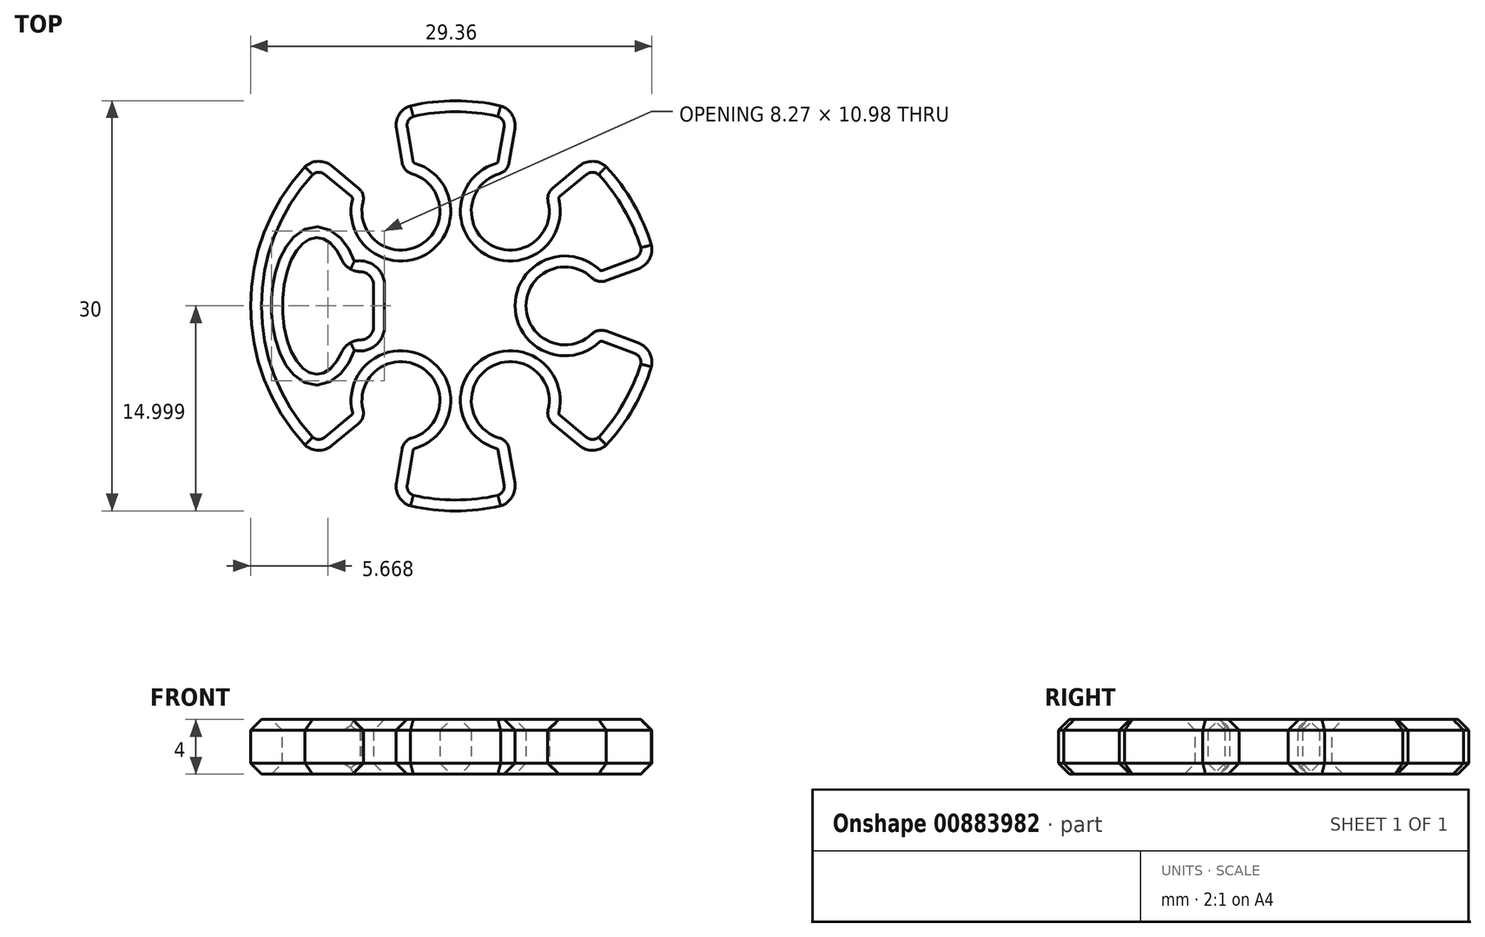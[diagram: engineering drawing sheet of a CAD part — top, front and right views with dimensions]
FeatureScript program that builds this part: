
annotation { "Feature Type Name" : "Feature", "Feature Type Description" : "" }
export const myFeature = defineFeature(function(context is Context, id is Id, definition is map)
    precondition{}
    {
        {
            var Q0;
            Q0=qCreatedBy(makeId("Top.planeOp"),FACE);
            var sketch = newSketch(context, id + "F0", { "sketchPlane" : qUnion([Q0])});
            skArc(sketch, "E0", {"start": v(9.97, 2.06) * mm, "mid": v(5.15, 0) * mm, "end": v(9.97, -2.06) * mm});
            skLineSegment(sketch, "E1", {"start": v(11.01, 1.84) * mm, "end": v(13.38, 2.73) * mm});
            skLineSegment(sketch, "E2", {"start": v(11.01, -1.84) * mm, "end": v(13.38, -2.73) * mm});
            skPoint(sketch, "E3.visualSharp", {"position": v(10.36, 1.6) * mm});
            skArc(sketch, "E3.filletArc", {"start": v(9.97, 2.06) * mm, "mid": v(10.46, 1.8) * mm, "end": v(11.01, 1.84) * mm});
            skPoint(sketch, "E4.visualSharp", {"position": v(14.65, 3.2) * mm});
            skArc(sketch, "E4.filletArc", {"start": v(13.38, 2.73) * mm, "mid": v(14.18, 3.42) * mm, "end": v(14.32, 4.46) * mm});
            skPoint(sketch, "E5.visualSharp", {"position": v(10.36, -1.6) * mm});
            skArc(sketch, "E5.filletArc", {"start": v(11.01, -1.84) * mm, "mid": v(10.46, -1.8) * mm, "end": v(9.97, -2.06) * mm});
            skPoint(sketch, "E6.visualSharp", {"position": v(14.65, -3.2) * mm});
            skArc(sketch, "E6.filletArc", {"start": v(14.32, -4.46) * mm, "mid": v(14.18, -3.42) * mm, "end": v(13.38, -2.73) * mm});
            skLineSegment(sketch, "E7", {"start": v(0, 0) * mm, "end": v(8, 0) * mm, "construction": true});
            skPoint(sketch, "E8.1.0", {"position": v(6.56, 8.17) * mm});
            skPoint(sketch, "E8.1.1", {"position": v(4.56, 14.3) * mm});
            skLineSegment(sketch, "E8.1.2", {"start": v(3.9, 10.46) * mm, "end": v(4.33, 12.95) * mm});
            skLineSegment(sketch, "E8.1.3", {"start": v(0, 0) * mm, "end": v(4, 6.93) * mm, "construction": true});
            skArc(sketch, "E8.1.4", {"start": v(3.2, 9.66) * mm, "mid": v(2.57, 4.46) * mm, "end": v(6.77, 7.6) * mm});
            skPoint(sketch, "E8.1.5", {"position": v(10.1, 11.1) * mm});
            skLineSegment(sketch, "E8.1.6", {"start": v(7.1, 8.61) * mm, "end": v(9.05, 10.23) * mm});
            skArc(sketch, "E8.1.7", {"start": v(11.02, 10.18) * mm, "mid": v(10.05, 10.57) * mm, "end": v(9.05, 10.23) * mm});
            skPoint(sketch, "E8.1.8", {"position": v(3.8, 9.77) * mm});
            skArc(sketch, "E8.1.9", {"start": v(4.33, 12.95) * mm, "mid": v(4.13, 13.98) * mm, "end": v(3.3, 14.63) * mm});
            skArc(sketch, "E8.1.10", {"start": v(3.2, 9.66) * mm, "mid": v(3.67, 9.96) * mm, "end": v(3.9, 10.46) * mm});
            skArc(sketch, "E8.1.11", {"start": v(7.1, 8.61) * mm, "mid": v(6.8, 8.16) * mm, "end": v(6.77, 7.6) * mm});
            skPoint(sketch, "E8.2.0", {"position": v(-3.8, 9.77) * mm});
            skPoint(sketch, "E8.2.1", {"position": v(-10.1, 11.1) * mm});
            skLineSegment(sketch, "E8.2.2", {"start": v(-7.1, 8.61) * mm, "end": v(-9.05, 10.23) * mm});
            skLineSegment(sketch, "E8.2.3", {"start": v(0, 0) * mm, "end": v(-4, 6.93) * mm, "construction": true});
            skArc(sketch, "E8.2.4", {"start": v(-6.77, 7.6) * mm, "mid": v(-2.57, 4.46) * mm, "end": v(-3.2, 9.66) * mm});
            skPoint(sketch, "E8.2.5", {"position": v(-4.56, 14.3) * mm});
            skLineSegment(sketch, "E8.2.6", {"start": v(-3.9, 10.46) * mm, "end": v(-4.33, 12.95) * mm});
            skArc(sketch, "E8.2.7", {"start": v(-3.3, 14.63) * mm, "mid": v(-4.13, 13.98) * mm, "end": v(-4.33, 12.95) * mm});
            skPoint(sketch, "E8.2.8", {"position": v(-6.56, 8.17) * mm});
            skArc(sketch, "E8.2.9", {"start": v(-9.05, 10.23) * mm, "mid": v(-10.05, 10.57) * mm, "end": v(-11.02, 10.18) * mm});
            skArc(sketch, "E8.2.10", {"start": v(-6.77, 7.6) * mm, "mid": v(-6.8, 8.16) * mm, "end": v(-7.1, 8.61) * mm});
            skArc(sketch, "E8.2.11", {"start": v(-3.9, 10.46) * mm, "mid": v(-3.67, 9.96) * mm, "end": v(-3.2, 9.66) * mm});
            skPoint(sketch, "E8.center", {"position": v(0, 0) * mm});
            skPoint(sketch, "E9.1.4.0", {"position": v(-4.56, -14.3) * mm});
            skLineSegment(sketch, "E9.2.4.0", {"start": v(-3.9, -10.46) * mm, "end": v(-4.33, -12.95) * mm});
            skLineSegment(sketch, "E9.5.4.0", {"start": v(0, 0) * mm, "end": v(-4, -6.93) * mm, "construction": true});
            skPoint(sketch, "E9.7.4.0", {"position": v(-6.56, -8.17) * mm});
            skArc(sketch, "E9.8.4.0", {"start": v(-3.2, -9.66) * mm, "mid": v(-2.58, -4.46) * mm, "end": v(-6.77, -7.6) * mm});
            skPoint(sketch, "E9.12.4.0", {"position": v(-10.1, -11.1) * mm});
            skLineSegment(sketch, "E9.13.4.0", {"start": v(-7.1, -8.61) * mm, "end": v(-9.05, -10.23) * mm});
            skArc(sketch, "E9.16.4.0", {"start": v(-11.02, -10.18) * mm, "mid": v(-10.05, -10.57) * mm, "end": v(-9.05, -10.23) * mm});
            skPoint(sketch, "E9.20.4.0", {"position": v(-3.8, -9.77) * mm});
            skArc(sketch, "E9.21.4.0", {"start": v(-4.33, -12.95) * mm, "mid": v(-4.13, -13.98) * mm, "end": v(-3.3, -14.63) * mm});
            skArc(sketch, "E9.25.4.0", {"start": v(-3.2, -9.66) * mm, "mid": v(-3.67, -9.96) * mm, "end": v(-3.9, -10.46) * mm});
            skArc(sketch, "E9.29.4.0", {"start": v(-7.1, -8.61) * mm, "mid": v(-6.8, -8.16) * mm, "end": v(-6.77, -7.6) * mm});
            skPoint(sketch, "E9.1.5.0", {"position": v(10.1, -11.1) * mm});
            skLineSegment(sketch, "E9.2.5.0", {"start": v(7.1, -8.61) * mm, "end": v(9.05, -10.23) * mm});
            skLineSegment(sketch, "E9.5.5.0", {"start": v(0, 0) * mm, "end": v(4, -6.93) * mm, "construction": true});
            skPoint(sketch, "E9.7.5.0", {"position": v(3.8, -9.77) * mm});
            skArc(sketch, "E9.8.5.0", {"start": v(6.77, -7.6) * mm, "mid": v(2.57, -4.46) * mm, "end": v(3.2, -9.66) * mm});
            skPoint(sketch, "E9.12.5.0", {"position": v(4.56, -14.3) * mm});
            skLineSegment(sketch, "E9.13.5.0", {"start": v(3.9, -10.46) * mm, "end": v(4.33, -12.95) * mm});
            skArc(sketch, "E9.16.5.0", {"start": v(3.3, -14.63) * mm, "mid": v(4.13, -13.98) * mm, "end": v(4.33, -12.95) * mm});
            skPoint(sketch, "E9.20.5.0", {"position": v(6.56, -8.17) * mm});
            skArc(sketch, "E9.21.5.0", {"start": v(9.05, -10.23) * mm, "mid": v(10.05, -10.57) * mm, "end": v(11.02, -10.18) * mm});
            skArc(sketch, "E9.25.5.0", {"start": v(6.77, -7.6) * mm, "mid": v(6.8, -8.16) * mm, "end": v(7.1, -8.61) * mm});
            skArc(sketch, "E9.29.5.0", {"start": v(3.9, -10.46) * mm, "mid": v(3.67, -9.96) * mm, "end": v(3.2, -9.66) * mm});
            skArc(sketch, "E10.trimOffspring", {"start": v(3.3, 14.63) * mm, "mid": v(0, 15) * mm, "end": v(-3.3, 14.63) * mm});
            skArc(sketch, "E11.trimOffspring", {"start": v(14.32, 4.46) * mm, "mid": v(13, 7.5) * mm, "end": v(11.02, 10.18) * mm});
            skArc(sketch, "E12.trimOffspring", {"start": v(11.02, -10.18) * mm, "mid": v(13, -7.5) * mm, "end": v(14.32, -4.46) * mm});
            skArc(sketch, "E13.trimOffspring", {"start": v(-3.3, -14.63) * mm, "mid": v(0, -15) * mm, "end": v(3.3, -14.63) * mm});
            skEllipticalArc(sketch, "E14", {});
            skLineSegment(sketch, "E15", {"start": v(-7, 2.5) * mm, "end": v(-6.96, 2.5) * mm});
            skLineSegment(sketch, "E16", {"start": v(-6, 1.5) * mm, "end": v(-6, -1.5) * mm});
            skLineSegment(sketch, "E17", {"start": v(-6.96, -2.5) * mm, "end": v(-7, -2.5) * mm});
            skArc(sketch, "E18", {"start": v(-11.02, 10.18) * mm, "mid": v(-15, 0) * mm, "end": v(-11.02, -10.18) * mm});
            skPoint(sketch, "E19.visualSharp", {"position": v(-8, 2.5) * mm});
            skArc(sketch, "E19.filletArc", {"start": v(-8.32, 3.38) * mm, "mid": v(-7.77, 2.74) * mm, "end": v(-6.96, 2.5) * mm});
            skPoint(sketch, "E20.visualSharp", {"position": v(-8, -2.5) * mm});
            skArc(sketch, "E20.filletArc", {"start": v(-6.96, -2.5) * mm, "mid": v(-7.77, -2.74) * mm, "end": v(-8.32, -3.38) * mm});
            skPoint(sketch, "E21.visualSharp", {"position": v(-6, -2.5) * mm});
            skArc(sketch, "E21.filletArc", {"start": v(-7, -2.5) * mm, "mid": v(-6.3, -2.2) * mm, "end": v(-6, -1.5) * mm});
            skPoint(sketch, "E22.visualSharp", {"position": v(-6, 2.5) * mm});
            skArc(sketch, "E22.filletArc", {"start": v(-6, 1.5) * mm, "mid": v(-6.3, 2.2) * mm, "end": v(-7, 2.5) * mm});
            const initialGuessF0  = {"E14": [-0.010165063509461116, 0, 0, -1, 0.005, 0.0025, 2.311980366410422, 0.8296122871793737]};
            skSetInitialGuess(sketch, initialGuessF0);
            skSolve(sketch);
        }
        {
            var Q0;
            Q0 = qSketchRegion(id + "F0", true);
            extrude(context, id + "F1", {"entities" : qUnion([Q0]), "depth" : 4 * mm, "offsetDistance" : 25 * mm});
        }
        {
            var Q0;
            Q0=makeQuery(id+"F1.opExtrude","CAP_FACE",FACE,{"disambiguationData":[OSD([sQuery(id+"F0.wireOp",EDGE,"E0"),sQuery(id+"F0.wireOp",EDGE,"E1"),sQuery(id+"F0.wireOp",EDGE,"E2"),sQuery(id+"F0.wireOp",EDGE,"E3.filletArc"),sQuery(id+"F0.wireOp",EDGE,"E4.filletArc"),sQuery(id+"F0.wireOp",EDGE,"E5.filletArc"),sQuery(id+"F0.wireOp",EDGE,"E6.filletArc"),sQuery(id+"F0.wireOp",EDGE,"E8.1.2"),sQuery(id+"F0.wireOp",EDGE,"E8.1.4"),sQuery(id+"F0.wireOp",EDGE,"E8.1.6"),sQuery(id+"F0.wireOp",EDGE,"E8.1.7"),sQuery(id+"F0.wireOp",EDGE,"E8.1.9"),sQuery(id+"F0.wireOp",EDGE,"E8.1.10"),sQuery(id+"F0.wireOp",EDGE,"E8.1.11"),sQuery(id+"F0.wireOp",EDGE,"E8.2.2"),sQuery(id+"F0.wireOp",EDGE,"E8.2.4"),sQuery(id+"F0.wireOp",EDGE,"E8.2.6"),sQuery(id+"F0.wireOp",EDGE,"E8.2.7"),sQuery(id+"F0.wireOp",EDGE,"E8.2.9"),sQuery(id+"F0.wireOp",EDGE,"E8.2.10"),sQuery(id+"F0.wireOp",EDGE,"E8.2.11"),sQuery(id+"F0.wireOp",EDGE,"E9.2.4.0"),sQuery(id+"F0.wireOp",EDGE,"E9.8.4.0"),sQuery(id+"F0.wireOp",EDGE,"E9.13.4.0"),sQuery(id+"F0.wireOp",EDGE,"E9.16.4.0"),sQuery(id+"F0.wireOp",EDGE,"E9.21.4.0"),sQuery(id+"F0.wireOp",EDGE,"E9.25.4.0"),sQuery(id+"F0.wireOp",EDGE,"E9.29.4.0"),sQuery(id+"F0.wireOp",EDGE,"E9.2.5.0"),sQuery(id+"F0.wireOp",EDGE,"E9.8.5.0"),sQuery(id+"F0.wireOp",EDGE,"E9.13.5.0"),sQuery(id+"F0.wireOp",EDGE,"E9.16.5.0"),sQuery(id+"F0.wireOp",EDGE,"E9.21.5.0"),sQuery(id+"F0.wireOp",EDGE,"E9.25.5.0"),sQuery(id+"F0.wireOp",EDGE,"E9.29.5.0"),sQuery(id+"F0.wireOp",EDGE,"E10.trimOffspring"),sQuery(id+"F0.wireOp",EDGE,"E11.trimOffspring"),sQuery(id+"F0.wireOp",EDGE,"E12.trimOffspring"),sQuery(id+"F0.wireOp",EDGE,"E13.trimOffspring"),sQuery(id+"F0.wireOp",EDGE,"E14"),sQuery(id+"F0.wireOp",EDGE,"E15"),sQuery(id+"F0.wireOp",EDGE,"E16"),sQuery(id+"F0.wireOp",EDGE,"E17"),sQuery(id+"F0.wireOp",EDGE,"E18"),sQuery(id+"F0.wireOp",EDGE,"E19.filletArc"),sQuery(id+"F0.wireOp",EDGE,"E20.filletArc"),sQuery(id+"F0.wireOp",EDGE,"E21.filletArc"),sQuery(id+"F0.wireOp",EDGE,"E22.filletArc")])],"isStart":false});
            var Q1;
            Q1=makeQuery(id+"F1.opExtrude","CAP_FACE",FACE,{"disambiguationData":[OSD([sQuery(id+"F0.wireOp",EDGE,"E0"),sQuery(id+"F0.wireOp",EDGE,"E1"),sQuery(id+"F0.wireOp",EDGE,"E2"),sQuery(id+"F0.wireOp",EDGE,"E3.filletArc"),sQuery(id+"F0.wireOp",EDGE,"E4.filletArc"),sQuery(id+"F0.wireOp",EDGE,"E5.filletArc"),sQuery(id+"F0.wireOp",EDGE,"E6.filletArc"),sQuery(id+"F0.wireOp",EDGE,"E8.1.2"),sQuery(id+"F0.wireOp",EDGE,"E8.1.4"),sQuery(id+"F0.wireOp",EDGE,"E8.1.6"),sQuery(id+"F0.wireOp",EDGE,"E8.1.7"),sQuery(id+"F0.wireOp",EDGE,"E8.1.9"),sQuery(id+"F0.wireOp",EDGE,"E8.1.10"),sQuery(id+"F0.wireOp",EDGE,"E8.1.11"),sQuery(id+"F0.wireOp",EDGE,"E8.2.2"),sQuery(id+"F0.wireOp",EDGE,"E8.2.4"),sQuery(id+"F0.wireOp",EDGE,"E8.2.6"),sQuery(id+"F0.wireOp",EDGE,"E8.2.7"),sQuery(id+"F0.wireOp",EDGE,"E8.2.9"),sQuery(id+"F0.wireOp",EDGE,"E8.2.10"),sQuery(id+"F0.wireOp",EDGE,"E8.2.11"),sQuery(id+"F0.wireOp",EDGE,"E9.2.4.0"),sQuery(id+"F0.wireOp",EDGE,"E9.8.4.0"),sQuery(id+"F0.wireOp",EDGE,"E9.13.4.0"),sQuery(id+"F0.wireOp",EDGE,"E9.16.4.0"),sQuery(id+"F0.wireOp",EDGE,"E9.21.4.0"),sQuery(id+"F0.wireOp",EDGE,"E9.25.4.0"),sQuery(id+"F0.wireOp",EDGE,"E9.29.4.0"),sQuery(id+"F0.wireOp",EDGE,"E9.2.5.0"),sQuery(id+"F0.wireOp",EDGE,"E9.8.5.0"),sQuery(id+"F0.wireOp",EDGE,"E9.13.5.0"),sQuery(id+"F0.wireOp",EDGE,"E9.16.5.0"),sQuery(id+"F0.wireOp",EDGE,"E9.21.5.0"),sQuery(id+"F0.wireOp",EDGE,"E9.25.5.0"),sQuery(id+"F0.wireOp",EDGE,"E9.29.5.0"),sQuery(id+"F0.wireOp",EDGE,"E10.trimOffspring"),sQuery(id+"F0.wireOp",EDGE,"E11.trimOffspring"),sQuery(id+"F0.wireOp",EDGE,"E12.trimOffspring"),sQuery(id+"F0.wireOp",EDGE,"E13.trimOffspring"),sQuery(id+"F0.wireOp",EDGE,"E14"),sQuery(id+"F0.wireOp",EDGE,"E15"),sQuery(id+"F0.wireOp",EDGE,"E16"),sQuery(id+"F0.wireOp",EDGE,"E17"),sQuery(id+"F0.wireOp",EDGE,"E18"),sQuery(id+"F0.wireOp",EDGE,"E19.filletArc"),sQuery(id+"F0.wireOp",EDGE,"E20.filletArc"),sQuery(id+"F0.wireOp",EDGE,"E21.filletArc"),sQuery(id+"F0.wireOp",EDGE,"E22.filletArc")])],"isStart":true});
            chamfer(context, id + "F2", {"entities" : qUnion([Q0, Q1]), "width" : .8 * mm, "tangentPropagation" : true});
        }
    });
